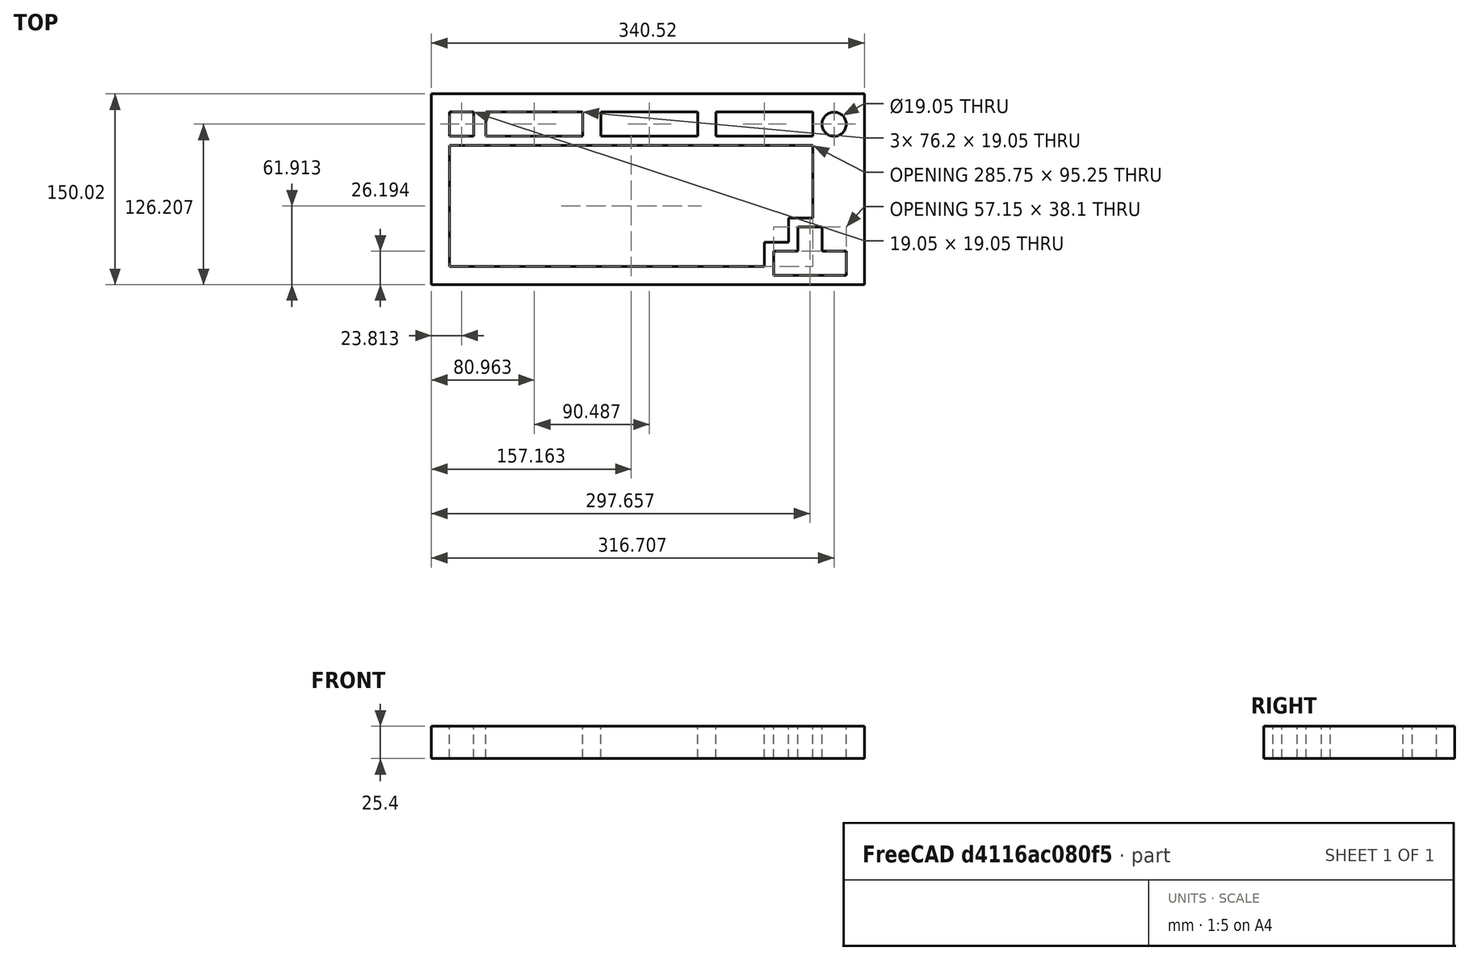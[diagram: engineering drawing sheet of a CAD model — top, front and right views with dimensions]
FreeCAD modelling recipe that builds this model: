
FCSTD DOCUMENT  (FreeCAD 0.19R19093 (Git))
Label: TopCase
License: All rights reserved
LicenseURL: http://en.wikipedia.org/wiki/All_rights_reserved
objects: Sketcher::SketchObject×2, Part::Extrusion×1
note: 3 computed .brp shape members not serialized (recipe doc carries the construction recipe); baked Part::Feature solids carry a one-line shape summary decoded from their .brp

FEATURE [Sketcher::SketchObject] Sketch
  sketch-geometry (48):
    g0: LineSegment StartX=-170.259 StartY=75.0094 StartZ=0 EndX=-170.259 EndY=-75.0094 EndZ=0
    g1: LineSegment StartX=-170.259 StartY=-75.0094 StartZ=0 EndX=170.259 EndY=-75.0094 EndZ=0
    g2: LineSegment StartX=170.259 StartY=-75.0094 StartZ=0 EndX=170.259 EndY=75.0094 EndZ=0
    g3: LineSegment StartX=170.259 StartY=75.0094 StartZ=0 EndX=-170.259 EndY=75.0094 EndZ=0
    g4: LineSegment StartX=-155.972 StartY=60.7219 StartZ=0 EndX=-136.922 EndY=60.7219 EndZ=0
    g5: LineSegment [constr] StartX=155.972 StartY=60.7219 StartZ=0 EndX=155.972 EndY=41.6719 EndZ=0
    g6: LineSegment StartX=155.972 StartY=-67.8656 StartZ=0 EndX=98.8219 EndY=-67.8656 EndZ=0
    g7: LineSegment StartX=-155.972 StartY=-60.7219 StartZ=0 EndX=-155.972 EndY=34.5281 EndZ=0
    g8: LineSegment StartX=155.972 StartY=-48.8156 StartZ=0 EndX=136.922 EndY=-48.8156 EndZ=0
    g9: LineSegment StartX=136.922 StartY=-48.8156 StartZ=0 EndX=136.922 EndY=-29.7656 EndZ=0
    g10: LineSegment StartX=136.922 StartY=-29.7656 StartZ=0 EndX=117.872 EndY=-29.7656 EndZ=0
    g11: LineSegment StartX=117.872 StartY=-29.7656 StartZ=0 EndX=117.872 EndY=-48.8156 EndZ=0
    g12: LineSegment StartX=117.872 StartY=-48.8156 StartZ=0 EndX=98.8219 EndY=-48.8156 EndZ=0
    g13: LineSegment StartX=98.8219 StartY=-48.8156 StartZ=0 EndX=98.8219 EndY=-67.8656 EndZ=0
    g14: LineSegment StartX=-155.972 StartY=-60.7219 StartZ=0 EndX=91.6781 EndY=-60.7219 EndZ=0
    g15: LineSegment StartX=91.6781 StartY=-60.7219 StartZ=0 EndX=91.6781 EndY=-41.6719 EndZ=0
    g16: LineSegment StartX=91.6781 StartY=-41.6719 StartZ=0 EndX=110.728 EndY=-41.6719 EndZ=0
    g17: LineSegment StartX=110.728 StartY=-41.6719 StartZ=0 EndX=110.728 EndY=-22.6219 EndZ=0
    g18: LineSegment StartX=110.728 StartY=-22.6219 StartZ=0 EndX=129.778 EndY=-22.6219 EndZ=0
    g19: LineSegment StartX=129.778 StartY=-22.6219 StartZ=0 EndX=129.778 EndY=34.5281 EndZ=0
    g20: LineSegment [constr] StartX=136.922 StartY=60.7219 StartZ=0 EndX=136.922 EndY=41.6719 EndZ=0
    g21: LineSegment [constr] StartX=136.922 StartY=41.6719 StartZ=0 EndX=155.972 EndY=41.6719 EndZ=0
    g22: LineSegment StartX=129.778 StartY=41.6719 StartZ=0 EndX=53.5781 EndY=41.6719 EndZ=0
    g23: LineSegment StartX=53.5781 StartY=41.6719 StartZ=0 EndX=53.5781 EndY=60.7219 EndZ=0
    g24: LineSegment StartX=39.2906 StartY=60.7219 StartZ=0 EndX=39.2906 EndY=41.6719 EndZ=0
    g25: LineSegment StartX=39.2906 StartY=41.6719 StartZ=0 EndX=-36.9094 EndY=41.6719 EndZ=0
    g26: LineSegment StartX=-36.9094 StartY=41.6719 StartZ=0 EndX=-36.9094 EndY=60.7219 EndZ=0
    g27: LineSegment StartX=-51.1969 StartY=60.7219 StartZ=0 EndX=-51.1969 EndY=41.6719 EndZ=0
    g28: LineSegment StartX=-51.1969 StartY=41.6719 StartZ=0 EndX=-127.397 EndY=41.6719 EndZ=0
    g29: LineSegment StartX=-127.397 StartY=41.6719 StartZ=0 EndX=-127.397 EndY=60.7219 EndZ=0
    g30: LineSegment StartX=-136.922 StartY=60.7219 StartZ=0 EndX=-136.922 EndY=41.6719 EndZ=0
    g31: LineSegment StartX=-136.922 StartY=41.6719 StartZ=0 EndX=-155.972 EndY=41.6719 EndZ=0
    g32: LineSegment StartX=-155.972 StartY=34.5281 StartZ=0 EndX=129.778 EndY=34.5281 EndZ=0
    g33: LineSegment StartX=129.778 StartY=41.6719 StartZ=0 EndX=129.778 EndY=60.7219 EndZ=0
    g34: LineSegment StartX=155.972 StartY=-48.8156 StartZ=0 EndX=155.972 EndY=-67.8656 EndZ=0
    g35: LineSegment StartX=-127.397 StartY=60.7219 StartZ=0 EndX=-51.1969 EndY=60.7219 EndZ=0
    g36: LineSegment StartX=-36.9094 StartY=60.7219 StartZ=0 EndX=39.2906 EndY=60.7219 EndZ=0
    g37: LineSegment StartX=-155.972 StartY=41.6719 StartZ=0 EndX=-155.972 EndY=60.7219 EndZ=0
    g38: LineSegment StartX=53.5781 StartY=60.7219 StartZ=0 EndX=129.778 EndY=60.7219 EndZ=0
    g39: LineSegment [constr] StartX=136.922 StartY=60.7219 StartZ=0 EndX=155.972 EndY=60.7219 EndZ=0
    g40: LineSegment [constr] StartX=-160.734 StartY=63.1044 StartZ=0 EndX=163.114 EndY=63.1044 EndZ=0
    g41: LineSegment [constr] StartX=163.114 StartY=63.1044 StartZ=0 EndX=163.114 EndY=-70.2481 EndZ=0
    g42: LineSegment [constr] StartX=163.114 StartY=-70.2481 StartZ=0 EndX=-160.734 EndY=-70.2481 EndZ=0
    g43: LineSegment [constr] StartX=-160.734 StartY=-70.2481 StartZ=0 EndX=-160.734 EndY=63.1044 EndZ=0
    g44: Circle CenterX=146.447 CenterY=51.1969 CenterZ=0 NormalX=0 NormalY=0 NormalZ=1 AngleXU=0 Radius=9.525
    g45: GeomPoint X=146.447 Y=60.7219 Z=0
    g46: LineSegment [constr] StartX=146.447 StartY=60.7219 StartZ=0 EndX=146.447 EndY=41.6719 EndZ=0
    g47: LineSegment [constr] StartX=136.922 StartY=51.1969 StartZ=0 EndX=155.972 EndY=51.1969 EndZ=0
  constraints (142):
    c: Coincident(g1,g0)
    c: Horizontal(g1)
    c: Vertical(g2)
    c: Coincident(g3,g2)
    c: Coincident(g3,g0)
    c: Equal(g1,g3)
    c: Equal(g0,g2)
    c: Symmetric(g0,g2,g-2)
    c: Symmetric(g0,g0,g-1)
    c: Coincident(g39,g5)
    c: Coincident(g34,g6)
    c: Coincident(g37,g4)
    c: Horizontal(g6)
    c: Vertical(g5)
    c: DistanceY(g34,g39) = 128.588
    c: Symmetric(g4,g39,g-2)
    c: Horizontal(g8)
    c: Coincident(g8,g9)
    c: Vertical(g9)
    c: Coincident(g9,g10)
    c: Horizontal(g10)
    c: Coincident(g10,g11)
    c: Vertical(g11)
    c: Coincident(g11,g12)
    c: Horizontal(g12)
    c: Coincident(g12,g13)
    c: Vertical(g13)
    c: Horizontal(g14)
    c: Vertical(g15)
    c: Coincident(g15,g16)
    c: Coincident(g16,g17)
    c: Vertical(g17)
    c: Coincident(g17,g18)
    c: Horizontal(g18)
    c: Coincident(g18,g19)
    c: Vertical(g19)
    c: Coincident(g20,g21)
    c: Horizontal(g21)
    c: PointOnObject(g20,g4)
    c: Horizontal(g22)
    c: Coincident(g22,g23)
    c: PointOnObject(g23,g4)
    c: Vertical(g23)
    c: Vertical(g24)
    c: Coincident(g24,g25)
    c: Horizontal(g25)
    c: Coincident(g25,g26)
    c: Vertical(g26)
    c: PointOnObject(g27,g4)
    c: Coincident(g27,g28)
    c: Horizontal(g28)
    c: Coincident(g28,g29)
    c: Vertical(g29)
    c: Vertical(g30)
    c: Coincident(g30,g31)
    c: Horizontal(g31)
    c: Horizontal(g32)
    c: Coincident(g19,g32)
    c: Coincident(g22,g33)
    c: PointOnObject(g33,g4)
    c: Vertical(g33)
    c: Coincident(g6,g13)
    c: Coincident(g15,g14)
    c: Coincident(g7,g14)
    c: Coincident(g5,g21)
    c: Coincident(g34,g8)
    c: Tangent(g5,g34)
    c: PointOnObject(g26,g4)
    c: PointOnObject(g24,g4)
    c: Vertical(g27)
    c: Vertical(g20)
    c: DistanceY(g26,g26) = 19.05
    c: DistanceY(g23,g23) = 19.05
    c: Equal(g20,g21)
    c: DistanceX(g22,g19) = 0
    c: DistanceX(g22,g20) = 7.14375
    c: Horizontal(g16)
    c: Vertical(g7)
    c: DistanceY(g13,g13) = 19.05
    c: DistanceY(g34,g34) = 19.05
    c: DistanceY(g9,g9) = 19.05
    c: DistanceX(g8,g8) = 19.05
    c: DistanceX(g12,g12) = 19.05
    c: DistanceX(g10,g10) = 19.05
    c: DistanceX(g14,g6) = 7.14375
    c: DistanceX(g16,g10) = 7.14375
    c: DistanceY(g11,g16) = 7.14375
    c: DistanceY(g10,g18) = 7.14375
    c: DistanceY(g6,g14) = 7.14375
    c: DistanceX(g14,g14) = 247.65
    c: DistanceX(g24,g23) = 14.2875
    c: DistanceX(g27,g26) = 14.2875
    c: Coincident(g4,g30)
    c: Coincident(g35,g29)
    c: Tangent(g4,g35)
    c: PointOnObject(g35,g27)
    c: PointOnObject(g36,g26)
    c: Tangent(g35,g36)
    c: Coincident(g7,g32)
    c: Coincident(g37,g31)
    c: Tangent(g7,g37)
    c: PointOnObject(g36,g24)
    c: PointOnObject(g38,g23)
    c: Tangent(g36,g38)
    c: PointOnObject(g38,g33)
    c: PointOnObject(g39,g20)
    c: Tangent(g38,g39)
    c: DistanceX(g4,g4) = 19.05
    c: DistanceY(g37,g37) = 19.05
    c: DistanceY(g29,g29) = 19.05
    c: DistanceY(g7,g31) = 7.14375
    c: DistanceX(g35,g35) = 76.2
    c: DistanceX(g4,g29) = 9.525
    c: DistanceX(g38,g38) = 76.2
    c: DistanceX(g36,g36) = 76.2
    c: DistanceX(g0,g7) = 14.2875
    c: DistanceY(g33,g2) = 14.2875
    c: DistanceY(g1,g6) = 7.14375
    c: Coincident(g40,g41)
    c: Coincident(g41,g42)
    c: Coincident(g42,g43)
    c: Coincident(g43,g40)
    c: Horizontal(g40)
    c: Horizontal(g42)
    c: Vertical(g41)
    c: Vertical(g43)
    c: DistanceX(g40,g4) = 4.7625
    c: DistanceY(g4,g40) = 2.38252
    c: DistanceY(g41,g6) = 2.38252
    c: DistanceX(g6,g41) = 7.14248
    c: PointOnObject(g45,g39)
    c: Coincident(g46,g45)
    c: PointOnObject(g46,g21)
    c: Vertical(g46)
    c: PointOnObject(g47,g20)
    c: PointOnObject(g47,g5)
    c: Horizontal(g47)
    c: PointOnObject(g44,g46)
    c: PointOnObject(g44,g47)
    c: DistanceY(g20,g47) = 9.525
    c: DistanceX(g20,g46) = 9.525
    c: PointOnObject(g45,g44)
FEATURE [Part::Extrusion] Extrude
  Base = -> Sketch
  Dir = (0,0,1)
  DirMode = 2
  FaceMakerClass = Part::FaceMakerBullseye
  LengthFwd = 25.4
  LengthRev = 0
  Solid = true
  Symmetric = false
FEATURE [Sketcher::SketchObject] Sketch001
  ExternalGeometry = -> [Extrude]
  MapMode = 5
  Placement = pos=(0,0,0) rot=(1,0,0;3.14159rad)
  Support = -> [Extrude]
  sketch-geometry (5):
    g0: LineSegment [constr] StartX=-170.259 StartY=75.0094 StartZ=0 EndX=-170.259 EndY=-75.0094 EndZ=0
    g1: LineSegment StartX=-168.953 StartY=69.3015 StartZ=0 EndX=169.184 EndY=69.3015 EndZ=0
    g2: LineSegment StartX=169.184 StartY=69.3015 StartZ=0 EndX=169.184 EndY=-70.3761 EndZ=0
    g3: LineSegment StartX=169.184 StartY=-70.3761 StartZ=0 EndX=-168.953 EndY=-70.3761 EndZ=0
    g4: LineSegment StartX=-168.953 StartY=-70.3761 StartZ=0 EndX=-168.953 EndY=69.3015 EndZ=0
  constraints (13):
    c: Vertical(g0)
    c: PointOnObject(g0,g-3)
    c: PointOnObject(g0,g-4)
    c: PointOnObject(g0,g-6)
    c: Coincident(g1,g2)
    c: Coincident(g2,g3)
    c: Coincident(g3,g4)
    c: Coincident(g4,g1)
    c: Horizontal(g1)
    c: Horizontal(g3)
    c: Vertical(g2)
    c: Vertical(g4)
    c: DistanceX(g1,g1) = 338.137
